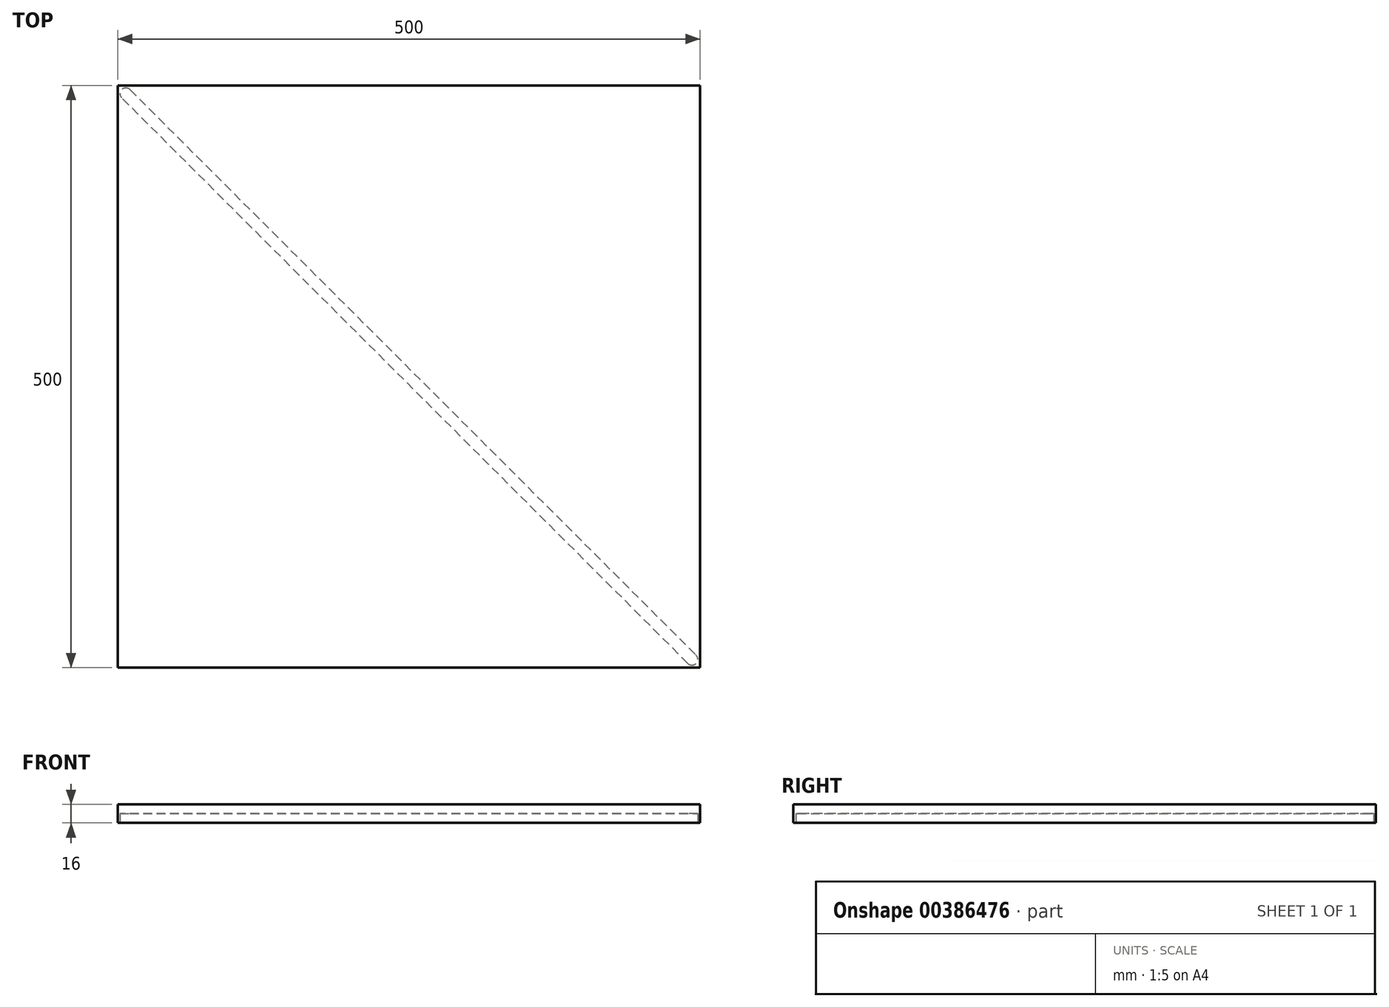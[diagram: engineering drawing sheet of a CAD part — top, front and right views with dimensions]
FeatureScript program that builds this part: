
annotation { "Feature Type Name" : "Feature", "Feature Type Description" : "" }
export const myFeature = defineFeature(function(context is Context, id is Id, definition is map)
    precondition{}
    {
        {
            var Q0;
            Q0=qCreatedBy(makeId("Top.planeOp"),FACE);
            var sketch = newSketch(context, id + "F0", { "sketchPlane" : qUnion([Q0])});
            skLineSegment(sketch, "E0.bottom", {"start": v(-239.4, -183.78) * mm, "end": v(260.6, -183.78) * mm});
            skLineSegment(sketch, "E0.top", {"start": v(-239.4, 316.22) * mm, "end": v(260.6, 316.22) * mm});
            skLineSegment(sketch, "E0.left", {"start": v(-239.4, -183.78) * mm, "end": v(-239.4, 316.22) * mm});
            skLineSegment(sketch, "E0.right", {"start": v(260.6, -183.78) * mm, "end": v(260.6, 316.22) * mm});
            skSolve(sketch);
        }
        {
            var Q0;
            Q0=makeQuery(id+"F0.imprint","IMPRINT",FACE,{"disambiguationData":[TD([[makeQuery(id+"F0.imprint","IMPRINT",EDGE,{"derivedFrom":sQuery(id+"F0.wireOp",EDGE,"E0.bottom")}),1.0]])]});
            extrude(context, id + "F1", {"entities" : qUnion([Q0]), "depth" : 16 * mm});
        }
        {
            var Q0;
            Q0=makeQuery(id+"F1.opExtrude","CAP_FACE",FACE,{"disambiguationData":[OSD([sQuery(id+"F0.wireOp",EDGE,"E0.bottom"),sQuery(id+"F0.wireOp",EDGE,"E0.top"),sQuery(id+"F0.wireOp",EDGE,"E0.left"),sQuery(id+"F0.wireOp",EDGE,"E0.right")])],"isStart":true});
            var sketch = newSketch(context, id + "F2", { "sketchPlane" : qUnion([Q0])});
            skLineSegment(sketch, "E1", {"start": v(-239.4, -316.22) * mm, "end": v(260.6, 183.78) * mm});
            skLineSegment(sketch, "E2", {"start": v(-157.95, -241.85) * mm, "end": v(257.07, 173.17) * mm});
            skLineSegment(sketch, "E3", {"start": v(257.07, 180.24) * mm, "end": v(257.07, 180.24) * mm});
            skLineSegment(sketch, "E4", {"start": v(250, 180.24) * mm, "end": v(-235.86, -305.62) * mm});
            skLineSegment(sketch, "E5", {"start": v(-235.86, -312.69) * mm, "end": v(-235.86, -312.69) * mm});
            skLineSegment(sketch, "E6", {"start": v(-228.79, -312.69) * mm, "end": v(-157.95, -241.85) * mm});
            skPoint(sketch, "E7.visualSharp", {"position": v(-232.32, -316.22) * mm});
            skArc(sketch, "E7.filletArc", {"start": v(-235.86, -312.69) * mm, "mid": v(-232.32, -314.15) * mm, "end": v(-228.79, -312.69) * mm});
            skPoint(sketch, "E8.visualSharp", {"position": v(-239.4, -309.15) * mm});
            skArc(sketch, "E8.filletArc", {"start": v(-235.86, -305.62) * mm, "mid": v(-237.32, -309.15) * mm, "end": v(-235.86, -312.69) * mm});
            skPoint(sketch, "E9.visualSharp", {"position": v(260.6, 176.7) * mm});
            skArc(sketch, "E9.filletArc", {"start": v(257.07, 173.17) * mm, "mid": v(258.53, 176.7) * mm, "end": v(257.07, 180.24) * mm});
            skPoint(sketch, "E10.visualSharp", {"position": v(253.53, 183.78) * mm});
            skArc(sketch, "E10.filletArc", {"start": v(257.07, 180.24) * mm, "mid": v(253.53, 181.7) * mm, "end": v(250, 180.24) * mm});
            skSolve(sketch);
        }
        {
            var Q0;
            Q0=makeQuery(id+"F2.imprint","IMPRINT",FACE,{"disambiguationData":[TD([[makeQuery(id+"F2.imprint","IMPRINT",EDGE,{"derivedFrom":sQuery(id+"F2.wireOp",EDGE,"E2")}),1.0]])]});
            var Q1;
            Q1=makeQuery(id+"F2.imprint","IMPRINT",FACE,{"disambiguationData":[TD([[makeQuery(id+"F2.imprint","IMPRINT",EDGE,{"derivedFrom":sQuery(id+"F2.wireOp",EDGE,"E4")}),1.0]])]});
            extrude(context, id + "F3", {"entities" : qUnion([Q0, Q1]), "operationType" : NewBodyOperationType.REMOVE, "oppositeDirection" : true, "depth" : 8 * mm});
        }
    });
